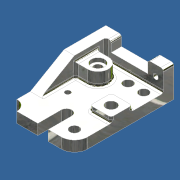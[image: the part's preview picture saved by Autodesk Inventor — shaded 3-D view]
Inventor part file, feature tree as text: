
AUTODESK INVENTOR PART (.ipt)
format: ipt  version: unknown  size: 371,712 bytes
history: native  units: in
note: dims shown in document units (in); Inventor stores cm internally (conversion verified against a paired STEP export)
features: sketch x13, extrude x7, hole x6, fillet x5
ambient origin geometry x8: Origin, YZ Plane, XZ Plane, XY Plane, X Axis, Y Axis, Z Axis, Center Point
bodies: Solid1 (feature_tree)
feature tree (31):
  extrude  "Extrusion1"  Depth=0.5in
  extrude  "Extrusion2"  TaperAngle=30.0deg  [1 undecoded]
  extrude  "Extrusion3"  Depth=0.93in
  extrude  "Extrusion4"  Depth=0.25in
  hole  "Hole1"  [1 undecoded]
  hole  "Hole2"  [1 undecoded]
  fillet  "Fillet1"  Radius=1.0in
  hole  "Hole3"  [1 undecoded]
  extrude  "Extrusion5"  Depth=0.375in
  hole  "Hole4"  [1 undecoded]
  extrude  "Extrusion6"  Depth=2.0in
  hole  "Hole5"  [1 undecoded]
  hole  "Hole6"  [1 undecoded]
  extrude  "Extrusion7"  Depth=0.5in
  fillet  "Fillet2"  Radius=0.25in
  fillet  "Fillet3"  Radius=0.5in
  fillet  "Fillet4"  Radius=0.94in
  fillet  "Fillet5"  Radius=0.56in
  sketch  "Sketch1"  dims[d0=4.75in d1=0.5in]
  sketch  "Sketch2"  dims[d2=3.25in d3=0.0in d4=30.0deg]
  sketch  "Sketch3"  dims[d5=2.0in d6=0.93in]
  sketch  "Sketch4"  dims[d7=0.5in d8=0.0in d9=0.25in]
  sketch  "Sketch5"  dims[d10=0.5in d11=1.75in]
  sketch  "Sketch6"  dims[d12=1.0in d13=0.5in d14=0.0in d15=1.0in]
  sketch  "Sketch7"  dims[d16=0.5in d17=0.0in d18=2.0in]
  sketch  "Sketch8"  dims[d19=0.93in]
  sketch  "Sketch9"  dims[d20=0.25in d21=0.75in d22=0.375in d23=0.25in d24=0.5635in d25=1.0in d26=0.8108in d27=0.375in]
  sketch  "Sketch10"  dims[d28=1.0in]
  sketch  "Sketch11"  dims[d29=0.25in d30=0.75in d31=0.375in d32=0.25in d33=0.5635in d34=1.0in d35=0.8108in d36=0.63in]
  sketch  "Sketch12"  dims[d37=0.44in d38=0.75in d39=0.375in d40=0.25in d41=0.5635in d42=1.0in d43=0.8108in d44=2.0in]
  sketch  "Sketch13"  dims[d45=1.0in d46=1.0in d47=0.5in d48=0.5in d49=0.25in d50=0.0in d51=0.5in d52=0.5in d53=0.75in d54=0.375in d55=0.25in d56=0.5635in d57=1.0in d58=0.8108in d59=0.94in d60=0.56in d61=1.0in d62=0.62in d63=0.0in d64=0.38in d65=0.75in d66=0.63in d67=0.18in d68=0.5635in d69=1.0in d70=0.8108in d71=0.5in d72=0.5in d73=0.75in d74=0.5in d75=0.44in d76=0.75in d77=0.63in d78=0.18in d79=0.5635in d80=1.0in d81=0.8108in d82=1.5in d83=1.12in d84=0.5in d85=0.62in d86=0.0in d87=0.125in d88=0.125in d89=0.125in d90=0.125in d91=0.5in]
note: 7 required parameter values undecoded (feature->parameter linkage not recoverable at this tier; creation-order binding heuristic only, values carry confidence <= 0.55)
